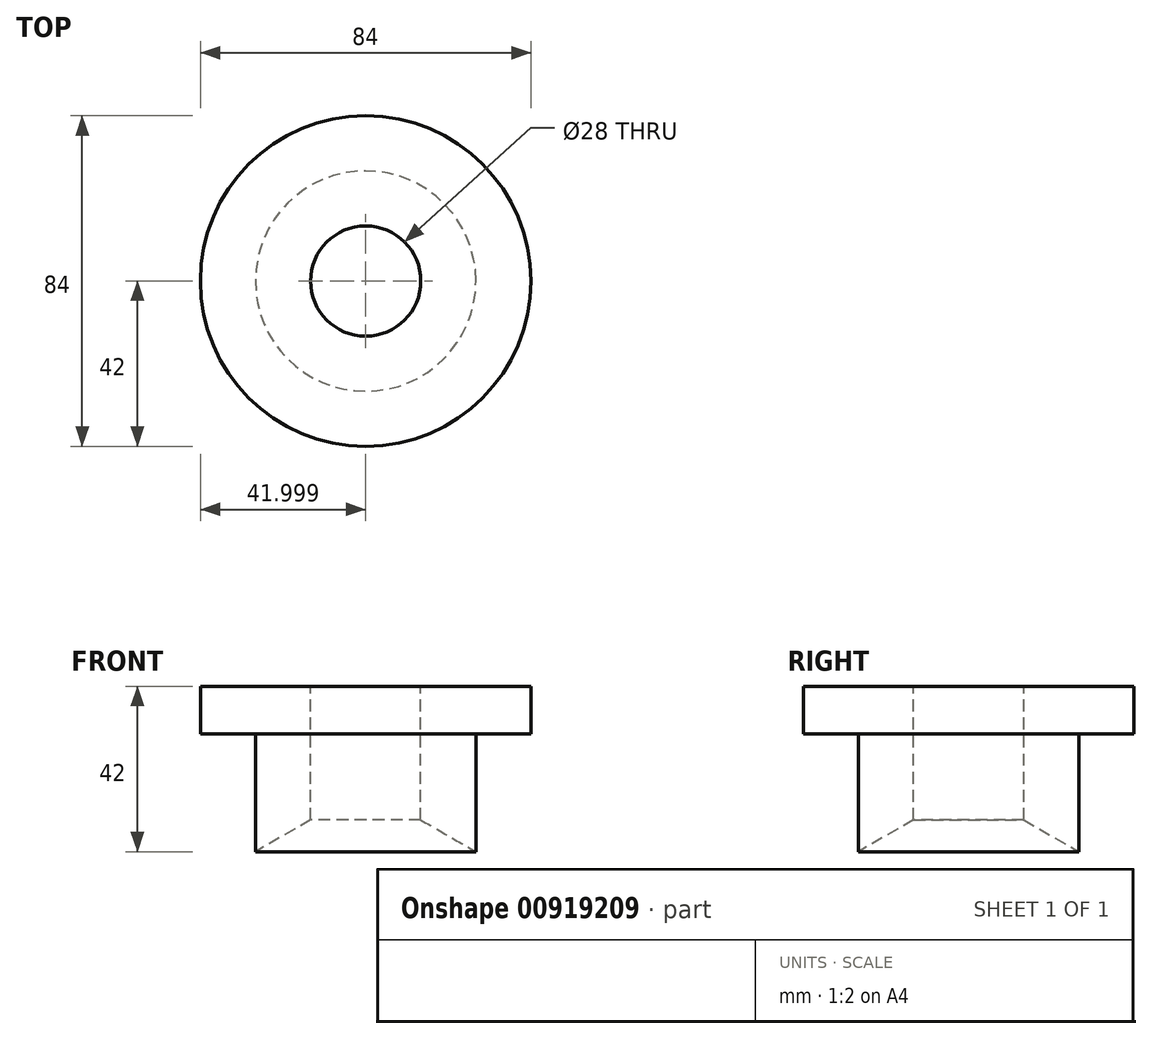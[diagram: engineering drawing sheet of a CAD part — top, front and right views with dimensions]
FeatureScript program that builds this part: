
annotation { "Feature Type Name" : "Feature", "Feature Type Description" : "" }
export const myFeature = defineFeature(function(context is Context, id is Id, definition is map)
    precondition{}
    {
        {
            var Q0;
            Q0=qCreatedBy(makeId("Front.planeOp"),FACE);
            var sketch = newSketch(context, id + "F0", { "sketchPlane" : qUnion([Q0])});
            skLineSegment(sketch, "E0", {"start": v(-103.01, 52.5) * mm, "end": v(-103.01, -65.4) * mm, "construction": true});
            skLineSegment(sketch, "E1", {"start": v(-103.01, -41.95) * mm, "end": v(-131.01, -41.95) * mm});
            skLineSegment(sketch, "E2", {"start": v(-131.01, -41.95) * mm, "end": v(-131.01, -11.95) * mm});
            skLineSegment(sketch, "E3", {"start": v(-131.01, -11.95) * mm, "end": v(-145.01, -11.95) * mm});
            skLineSegment(sketch, "E4", {"start": v(-145.01, -11.95) * mm, "end": v(-145.01, 0.05) * mm});
            skLineSegment(sketch, "E5", {"start": v(-145.01, 0.05) * mm, "end": v(-103.01, 0.05) * mm});
            skLineSegment(sketch, "E6", {"start": v(-131.01, -41.95) * mm, "end": v(-117.01, -33.87) * mm});
            skLineSegment(sketch, "E7", {"start": v(-117.01, 0.05) * mm, "end": v(-117.01, -33.87) * mm});
            skLineSegment(sketch, "E8", {"start": v(-89.02, -17.7) * mm, "end": v(-88.92, -17.65) * mm});
            skSolve(sketch);
        }
        {
            var Q0;
            Q0=makeQuery(id+"F0.imprint","IMPRINT",FACE,{"disambiguationData":[TD([[makeQuery(id+"F0.imprint","IMPRINT",EDGE,{"derivedFrom":sQuery(id+"F0.wireOp",EDGE,"E2")}),-1.0]])]});
            var Q1;
            Q1=sQuery(id+"F0.wireOp",EDGE,"E0");
            revolve(context, id + "F1", {"surfaceOperationType" : NewSurfaceOperationType.NEW, "entities" : qUnion([Q0]), "axis" : qUnion([Q1]), "revolveType" : RevolveType.FULL});
        }
    });
